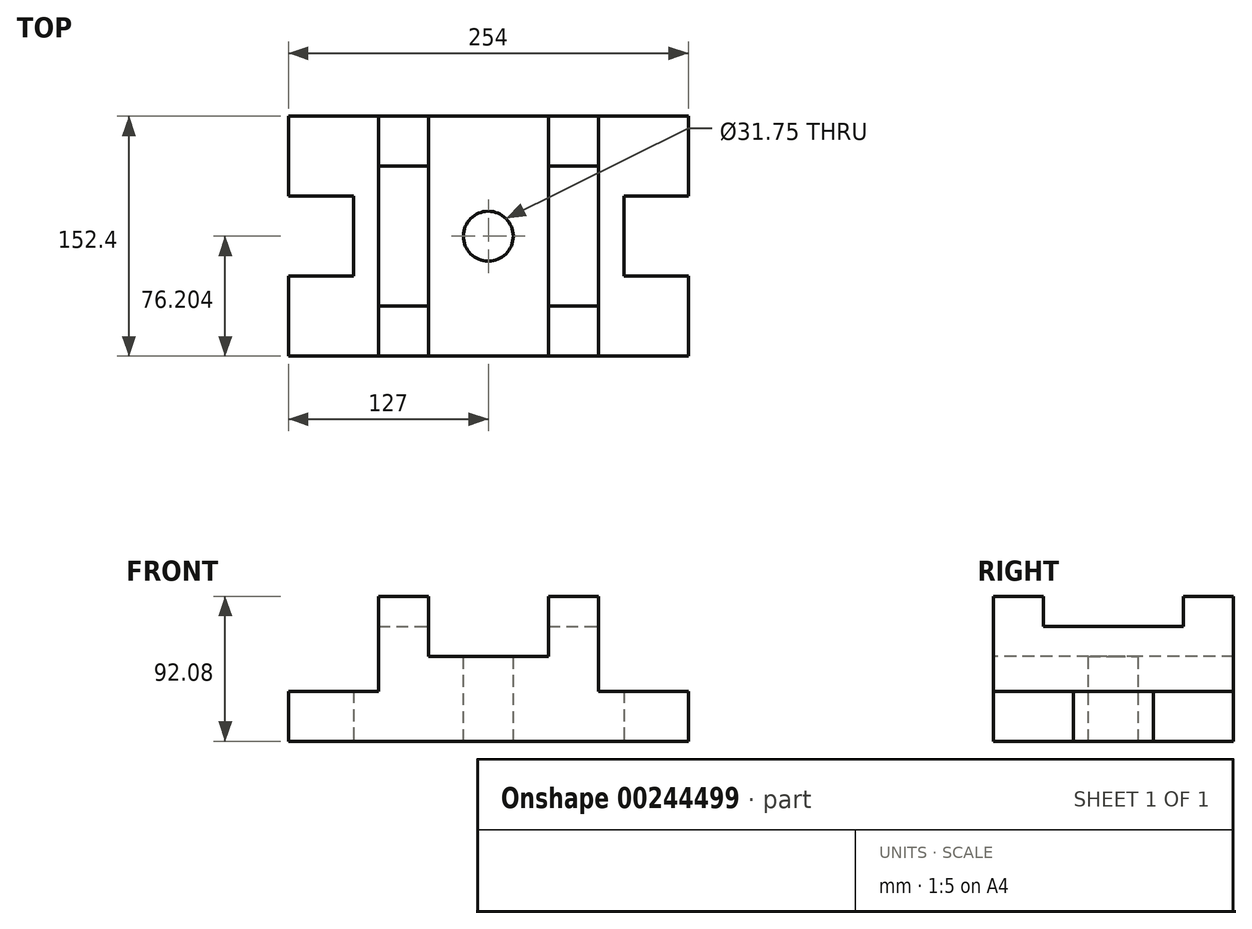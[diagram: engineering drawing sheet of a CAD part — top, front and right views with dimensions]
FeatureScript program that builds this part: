
annotation { "Feature Type Name" : "Feature", "Feature Type Description" : "" }
export const myFeature = defineFeature(function(context is Context, id is Id, definition is map)
    precondition{}
    {
        {
            var Q0;
            Q0=qCreatedBy(makeId("Top.planeOp"),FACE);
            var sketch = newSketch(context, id + "F0", { "sketchPlane" : qUnion([Q0])});
            skLineSegment(sketch, "E0", {"start": v(-187.9, 79.71) * mm, "end": v(66.1, 79.71) * mm});
            skLineSegment(sketch, "E1", {"start": v(-187.9, 79.71) * mm, "end": v(-187.9, 28.91) * mm});
            skLineSegment(sketch, "E2", {"start": v(-187.9, 28.91) * mm, "end": v(-146.63, 28.91) * mm});
            skLineSegment(sketch, "E3", {"start": v(-146.63, 28.91) * mm, "end": v(-146.63, -21.89) * mm});
            skLineSegment(sketch, "E4", {"start": v(-146.63, -21.89) * mm, "end": v(-187.9, -21.89) * mm});
            skLineSegment(sketch, "E5", {"start": v(-187.9, -21.89) * mm, "end": v(-187.9, -72.69) * mm});
            skLineSegment(sketch, "E6", {"start": v(66.1, -72.69) * mm, "end": v(66.1, -21.89) * mm});
            skLineSegment(sketch, "E7", {"start": v(66.1, -21.89) * mm, "end": v(25.16, -21.89) * mm});
            skLineSegment(sketch, "E8", {"start": v(25.16, -21.89) * mm, "end": v(25.16, 28.91) * mm});
            skLineSegment(sketch, "E9", {"start": v(24.82, 28.91) * mm, "end": v(66.1, 28.91) * mm});
            skLineSegment(sketch, "E10", {"start": v(66.1, 79.71) * mm, "end": v(66.1, 28.91) * mm});
            skLineSegment(sketch, "E11", {"start": v(-187.9, -72.69) * mm, "end": v(66.1, -72.69) * mm});
            skSolve(sketch);
        }
        {
            var Q0;
            Q0 = qSketchRegion(id + "F0", true);
            extrude(context, id + "F1", {"entities" : qUnion([Q0]), "depth" : 31.75 * mm});
        }
        {
            var Q0;
            Q0=makeQuery(id+"F1.opExtrude","CAP_FACE",FACE,{"disambiguationData":[OSD([sQuery(id+"F0.wireOp",EDGE,"E0"),sQuery(id+"F0.wireOp",EDGE,"E1"),sQuery(id+"F0.wireOp",EDGE,"E2"),sQuery(id+"F0.wireOp",EDGE,"E3"),sQuery(id+"F0.wireOp",EDGE,"E4"),sQuery(id+"F0.wireOp",EDGE,"E5"),sQuery(id+"F0.wireOp",EDGE,"E6"),sQuery(id+"F0.wireOp",EDGE,"E7"),sQuery(id+"F0.wireOp",EDGE,"E8"),sQuery(id+"F0.wireOp",EDGE,"E9"),sQuery(id+"F0.wireOp",EDGE,"E10"),sQuery(id+"F0.wireOp",EDGE,"E11")])],"isStart":false});
            var sketch = newSketch(context, id + "F2", { "sketchPlane" : qUnion([Q0])});
            skLineSegment(sketch, "E12.bottom", {"start": v(-130.76, -72.69) * mm, "end": v(8.94, -72.69) * mm});
            skLineSegment(sketch, "E12.top", {"start": v(-130.76, 79.71) * mm, "end": v(8.94, 79.71) * mm});
            skLineSegment(sketch, "E12.left", {"start": v(-130.76, -72.69) * mm, "end": v(-130.76, 79.71) * mm});
            skLineSegment(sketch, "E12.right", {"start": v(8.94, -72.69) * mm, "end": v(8.94, 79.71) * mm});
            skSolve(sketch);
        }
        {
            var Q0;
            Q0 = qSketchRegion(id + "F2", true);
            extrude(context, id + "F3", {"entities" : qUnion([Q0]), "operationType" : NewBodyOperationType.ADD, "depth" : 22.22 * mm});
        }
        {
            var Q0;
            Q0=makeQuery(id+"F3.opExtrude","CAP_FACE",FACE,{"disambiguationData":[OSD([sQuery(id+"F2.wireOp",EDGE,"E12.bottom"),sQuery(id+"F2.wireOp",EDGE,"E12.top"),sQuery(id+"F2.wireOp",EDGE,"E12.left"),sQuery(id+"F2.wireOp",EDGE,"E12.right")])],"isStart":false});
            var sketch = newSketch(context, id + "F4", { "sketchPlane" : qUnion([Q0])});
            skLineSegment(sketch, "E13", {"start": v(-130.76, 79.71) * mm, "end": v(-99, 79.71) * mm});
            skLineSegment(sketch, "E14", {"start": v(-99, 79.71) * mm, "end": v(-99, -72.69) * mm});
            skLineSegment(sketch, "E15", {"start": v(-99, -72.69) * mm, "end": v(-130.76, -72.69) * mm});
            skLineSegment(sketch, "E16", {"start": v(8.94, 79.71) * mm, "end": v(-22.8, 79.71) * mm});
            skLineSegment(sketch, "E17", {"start": v(-22.8, 79.71) * mm, "end": v(-22.8, -72.69) * mm});
            skLineSegment(sketch, "E18", {"start": v(-22.8, -72.69) * mm, "end": v(8.94, -72.69) * mm});
            skLineSegment(sketch, "E19", {"start": v(8.94, -72.69) * mm, "end": v(8.94, 79.71) * mm});
            skLineSegment(sketch, "E20", {"start": v(-130.76, 79.71) * mm, "end": v(-130.76, -72.69) * mm});
            skSolve(sketch);
        }
        {
            var Q0;
            Q0 = qSketchRegion(id + "F4", true);
            extrude(context, id + "F5", {"entities" : qUnion([Q0]), "operationType" : NewBodyOperationType.ADD, "depth" : 19.05 * mm});
        }
        {
            var Q0;
            Q0=makeQuery(id+"F5.opExtrude","CAP_FACE",FACE,{"disambiguationData":[OSD([sQuery(id+"F4.wireOp",EDGE,"E13"),sQuery(id+"F4.wireOp",EDGE,"E14"),sQuery(id+"F4.wireOp",EDGE,"E15"),sQuery(id+"F4.wireOp",EDGE,"E20")])],"isStart":false});
            var sketch = newSketch(context, id + "F6", { "sketchPlane" : qUnion([Q0])});
            skLineSegment(sketch, "E21", {"start": v(-130.76, -72.69) * mm, "end": v(-130.76, -40.94) * mm});
            skLineSegment(sketch, "E22", {"start": v(-130.76, -40.94) * mm, "end": v(-99, -40.94) * mm});
            skLineSegment(sketch, "E23", {"start": v(-99, -40.94) * mm, "end": v(-99, -72.69) * mm});
            skLineSegment(sketch, "E24", {"start": v(-99, -72.69) * mm, "end": v(-130.76, -72.69) * mm});
            skLineSegment(sketch, "E25", {"start": v(-130.76, 79.71) * mm, "end": v(-130.76, 47.96) * mm});
            skLineSegment(sketch, "E26", {"start": v(-130.76, 47.96) * mm, "end": v(-99, 47.96) * mm});
            skLineSegment(sketch, "E27", {"start": v(-99, 47.96) * mm, "end": v(-99, 79.71) * mm});
            skLineSegment(sketch, "E28", {"start": v(-99, 79.71) * mm, "end": v(-130.76, 79.71) * mm});
            skSolve(sketch);
        }
        {
            var Q0;
            Q0 = qSketchRegion(id + "F6", true);
            extrude(context, id + "F7", {"entities" : qUnion([Q0]), "operationType" : NewBodyOperationType.ADD, "depth" : 19.05 * mm});
        }
        {
            var Q0;
            Q0=makeQuery(id+"F5.opExtrude","CAP_FACE",FACE,{"disambiguationData":[OSD([sQuery(id+"F4.wireOp",EDGE,"E16"),sQuery(id+"F4.wireOp",EDGE,"E17"),sQuery(id+"F4.wireOp",EDGE,"E18"),sQuery(id+"F4.wireOp",EDGE,"E19")])],"isStart":false});
            var sketch = newSketch(context, id + "F8", { "sketchPlane" : qUnion([Q0])});
            skLineSegment(sketch, "E29", {"start": v(-22.8, 79.71) * mm, "end": v(-22.8, 47.96) * mm});
            skLineSegment(sketch, "E30", {"start": v(-22.8, 47.96) * mm, "end": v(8.94, 47.96) * mm});
            skLineSegment(sketch, "E31", {"start": v(8.94, 47.96) * mm, "end": v(8.94, 79.71) * mm});
            skLineSegment(sketch, "E32", {"start": v(8.94, 79.71) * mm, "end": v(-22.8, 79.71) * mm});
            skLineSegment(sketch, "E33", {"start": v(-22.8, -72.69) * mm, "end": v(-22.8, -40.94) * mm});
            skLineSegment(sketch, "E34", {"start": v(-22.8, -40.94) * mm, "end": v(8.94, -40.94) * mm});
            skLineSegment(sketch, "E35", {"start": v(8.94, -40.94) * mm, "end": v(8.94, -72.69) * mm});
            skLineSegment(sketch, "E36", {"start": v(8.94, -72.69) * mm, "end": v(-22.8, -72.69) * mm});
            skSolve(sketch);
        }
        {
            var Q0;
            Q0 = qSketchRegion(id + "F8", true);
            extrude(context, id + "F9", {"entities" : qUnion([Q0]), "operationType" : NewBodyOperationType.ADD, "depth" : 19.05 * mm});
        }
        {
            var Q0;
            Q0=makeQuery(id+"F3.opExtrude","CAP_FACE",FACE,{"disambiguationData":[OSD([sQuery(id+"F2.wireOp",EDGE,"E12.bottom"),sQuery(id+"F2.wireOp",EDGE,"E12.top"),sQuery(id+"F2.wireOp",EDGE,"E12.left"),sQuery(id+"F2.wireOp",EDGE,"E12.right")])],"isStart":false});
            var sketch = newSketch(context, id + "F10", { "sketchPlane" : qUnion([Q0])});
            skCircle(sketch, "E37", {"center": v(-60.9, 3.51) * mm, "radius": 15.88 * mm});
            skSolve(sketch);
        }
        {
            var Q0;
            Q0=sQuery(id+"F10.wireOp",VERTEX,"E37.center");
            var Q1;
            Q1=makeQuery(id+"F1.opExtrude","SWEPT_BODY",BODY,{"disambiguationData":[OSD([sQuery(id+"F0.wireOp",EDGE,"E0"),sQuery(id+"F0.wireOp",EDGE,"E1"),sQuery(id+"F0.wireOp",EDGE,"E2"),sQuery(id+"F0.wireOp",EDGE,"E3"),sQuery(id+"F0.wireOp",EDGE,"E4"),sQuery(id+"F0.wireOp",EDGE,"E5"),sQuery(id+"F0.wireOp",EDGE,"E6"),sQuery(id+"F0.wireOp",EDGE,"E7"),sQuery(id+"F0.wireOp",EDGE,"E8"),sQuery(id+"F0.wireOp",EDGE,"E9"),sQuery(id+"F0.wireOp",EDGE,"E10"),sQuery(id+"F0.wireOp",EDGE,"E11")])]});
            hole(context, id + "F11", {"style" : HoleStyle.SIMPLE, "endStyle" : HoleEndStyle.THROUGH, "holeDiameter" : 31.75 * mm, "tappedDepth" : 12.7 * mm, "tapClearance" : 3, "locations" : qUnion([Q0]), "scope" : qUnion([Q1])});
        }
    });
